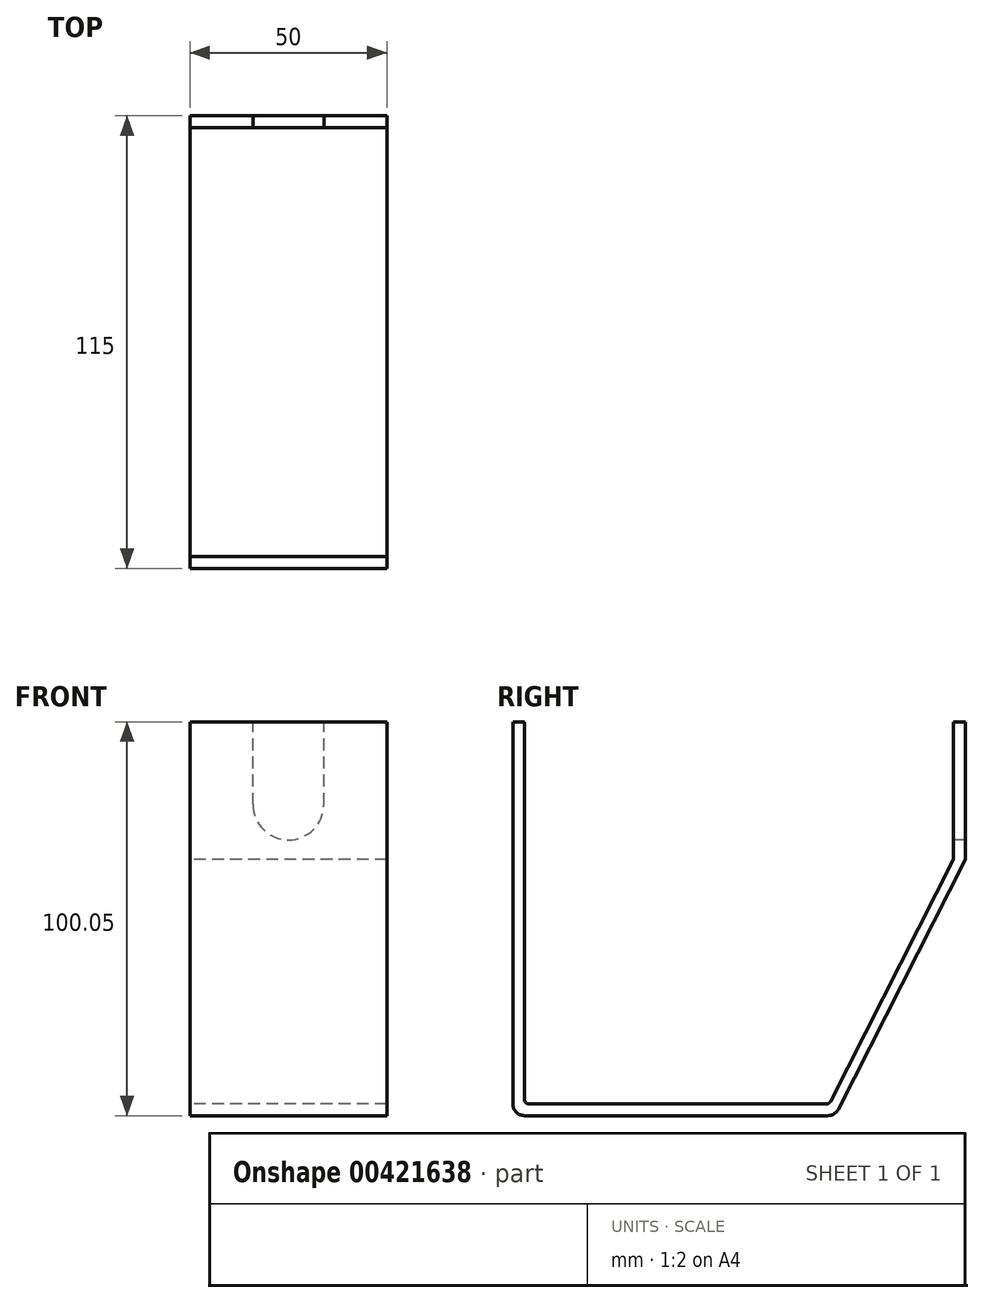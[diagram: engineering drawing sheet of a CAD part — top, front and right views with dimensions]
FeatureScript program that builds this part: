
annotation { "Feature Type Name" : "Feature", "Feature Type Description" : "" }
export const myFeature = defineFeature(function(context is Context, id is Id, definition is map)
    precondition{}
    {
        {
            var Q0;
            Q0=qCreatedBy(makeId("Front.planeOp"),FACE);
            var sketch = newSketch(context, id + "F0", { "sketchPlane" : qUnion([Q0])});
            skPoint(sketch, "E0.middle", {"position": v(0, 0) * mm});
            skPoint(sketch, "E1.orphan", {"position": v(0, 49.82) * mm});
            skLineSegment(sketch, "E2", {"start": v(25, 87.82) * mm, "end": v(25, -16.68) * mm});
            skCircle(sketch, "E3", {"center": v(0, 49.82) * mm, "radius": 5 * mm});
            skLineSegment(sketch, "E4", {"start": v(-25, -16.68) * mm, "end": v(25, -16.68) * mm});
            skLineSegment(sketch, "E5", {"start": v(-25, 87.82) * mm, "end": v(-25, -16.68) * mm});
            skLineSegment(sketch, "E6", {"start": v(-25, 87.82) * mm, "end": v(25, 87.82) * mm});
            skLineSegment(sketch, "E7", {"start": v(0, 98.86) * mm, "end": v(0, -48.72) * mm, "construction": true});
            skPoint(sketch, "E8.orphan", {"position": v(0, 87.82) * mm});
            skLineSegment(sketch, "E9", {"start": v(-38.2, 62.82) * mm, "end": v(31.99, 62.82) * mm, "construction": true});
            skLineSegment(sketch, "E10", {"start": v(-37.85, 66.82) * mm, "end": v(33.86, 66.82) * mm, "construction": true});
            skCircle(sketch, "E11", {"center": v(0, 66.82) * mm, "radius": 9 * mm});
            skLineSegment(sketch, "E12", {"start": v(-9, 66.82) * mm, "end": v(-9, 87.82) * mm});
            skLineSegment(sketch, "E13", {"start": v(9, 66.82) * mm, "end": v(9, 87.82) * mm});
            skLineSegment(sketch, "E14", {"start": v(-32.52, 49.82) * mm, "end": v(35.7, 49.82) * mm, "construction": true});
            skLineSegment(sketch, "E15", {"start": v(-34.31, 52.82) * mm, "end": v(40.83, 52.82) * mm, "construction": true});
            skSolve(sketch);
        }
        {
            var Q0;
            Q0=qCreatedBy(makeId("Right.planeOp"),FACE);
            var sketch = newSketch(context, id + "F1", { "sketchPlane" : qUnion([Q0])});
            skLineSegment(sketch, "E16", {"start": v(-90.92, -8.23) * mm, "end": v(-90.92, 87.82) * mm});
            skLineSegment(sketch, "E17", {"start": v(-93.92, 87.82) * mm, "end": v(-93.92, -9.23) * mm});
            skLineSegment(sketch, "E18", {"start": v(18.08, 52.82) * mm, "end": v(18.08, 87.82) * mm});
            skLineSegment(sketch, "E19", {"start": v(21.08, 87.82) * mm, "end": v(21.08, 52.82) * mm});
            skLineSegment(sketch, "E20", {"start": v(-109.87, 87.82) * mm, "end": v(52.46, 87.82) * mm, "construction": true});
            skLineSegment(sketch, "E21", {"start": v(18.08, 87.82) * mm, "end": v(21.08, 87.82) * mm});
            skLineSegment(sketch, "E22", {"start": v(-89.92, -9.23) * mm, "end": v(-14.14, -9.23) * mm});
            skPoint(sketch, "E23.orphan", {"position": v(0, -16.68) * mm});
            skLineSegment(sketch, "E24", {"start": v(-90.92, -12.23) * mm, "end": v(-13.9, -12.23) * mm});
            skLineSegment(sketch, "E25", {"start": v(-93.92, 87.82) * mm, "end": v(-90.92, 87.82) * mm});
            skLineSegment(sketch, "E26", {"start": v(0, 87.82) * mm, "end": v(0, -45.99) * mm, "construction": true});
            skLineSegment(sketch, "E27", {"start": v(0, 66.82) * mm, "end": v(68.6, 66.82) * mm, "construction": true});
            skLineSegment(sketch, "E28", {"start": v(0, 52.82) * mm, "end": v(43.04, 52.82) * mm, "construction": true});
            skLineSegment(sketch, "E29", {"start": v(18.08, 52.82) * mm, "end": v(-13.25, -8.68) * mm});
            skLineSegment(sketch, "E30", {"start": v(0, 27.58) * mm, "end": v(18.85, 17.97) * mm, "construction": true});
            skLineSegment(sketch, "E31", {"start": v(21.08, 52.82) * mm, "end": v(-11.22, -10.6) * mm});
            skPoint(sketch, "E32.visualSharp", {"position": v(-90.92, -9.23) * mm});
            skArc(sketch, "E32.filletArc", {"start": v(-90.92, -8.23) * mm, "mid": v(-90.62, -8.94) * mm, "end": v(-89.92, -9.23) * mm});
            skPoint(sketch, "E33.visualSharp", {"position": v(-13.53, -9.23) * mm});
            skArc(sketch, "E33.filletArc", {"start": v(-14.14, -9.23) * mm, "mid": v(-13.62, -9.08) * mm, "end": v(-13.25, -8.68) * mm});
            skPoint(sketch, "E34.visualSharp", {"position": v(-12.06, -12.23) * mm});
            skArc(sketch, "E34.filletArc", {"start": v(-13.9, -12.23) * mm, "mid": v(-12.33, -11.79) * mm, "end": v(-11.22, -10.6) * mm});
            skPoint(sketch, "E35.visualSharp", {"position": v(-93.92, -12.23) * mm});
            skArc(sketch, "E35.filletArc", {"start": v(-93.92, -9.23) * mm, "mid": v(-93.04, -11.35) * mm, "end": v(-90.92, -12.23) * mm});
            skSolve(sketch);
        }
        {
            var Q0;
            Q0=makeQuery(id+"F1.imprint","IMPRINT",FACE,{"disambiguationData":[TD([[makeQuery(id+"F1.imprint","IMPRINT",EDGE,{"derivedFrom":sQuery(id+"F1.wireOp",EDGE,"E16")}),1.0]])]});
            extrude(context, id + "F2", {"entities" : qUnion([Q0]), "endBound" : BoundingType.SYMMETRIC, "depth" : 50 * mm});
        }
        {
            var Q0;
            {var subQ0=sQuery(id+"F0.wireOp",EDGE,"E11");var subQ1=makeQuery(id+"F0.imprint","INTERSECT",VERTEX,{"derivedFrom":[subQ0,sQuery(id+"F0.wireOp",EDGE,"E12")]});Q0=makeQuery(id+"F0.imprint","IMPRINT",FACE,{"disambiguationData":[TD([[makeQuery(id+"F0.imprint","IMPRINT",EDGE,{"disambiguationData":[TD([[subQ1,1.0]])],"derivedFrom":subQ0}),1.0]])]});}
            var Q1;
            {var subQ0=sQuery(id+"F0.wireOp",EDGE,"E12");Q1=makeQuery(id+"F0.imprint","IMPRINT",FACE,{"disambiguationData":[TD([[makeQuery(id+"F0.imprint","IMPRINT",EDGE,{"derivedFrom":subQ0}),-1.0]])]});}
            extrude(context, id + "F3", {"entities" : qUnion([Q0, Q1]), "operationType" : NewBodyOperationType.REMOVE, "oppositeDirection" : true, "depth" : 25 * mm});
        }
    });
